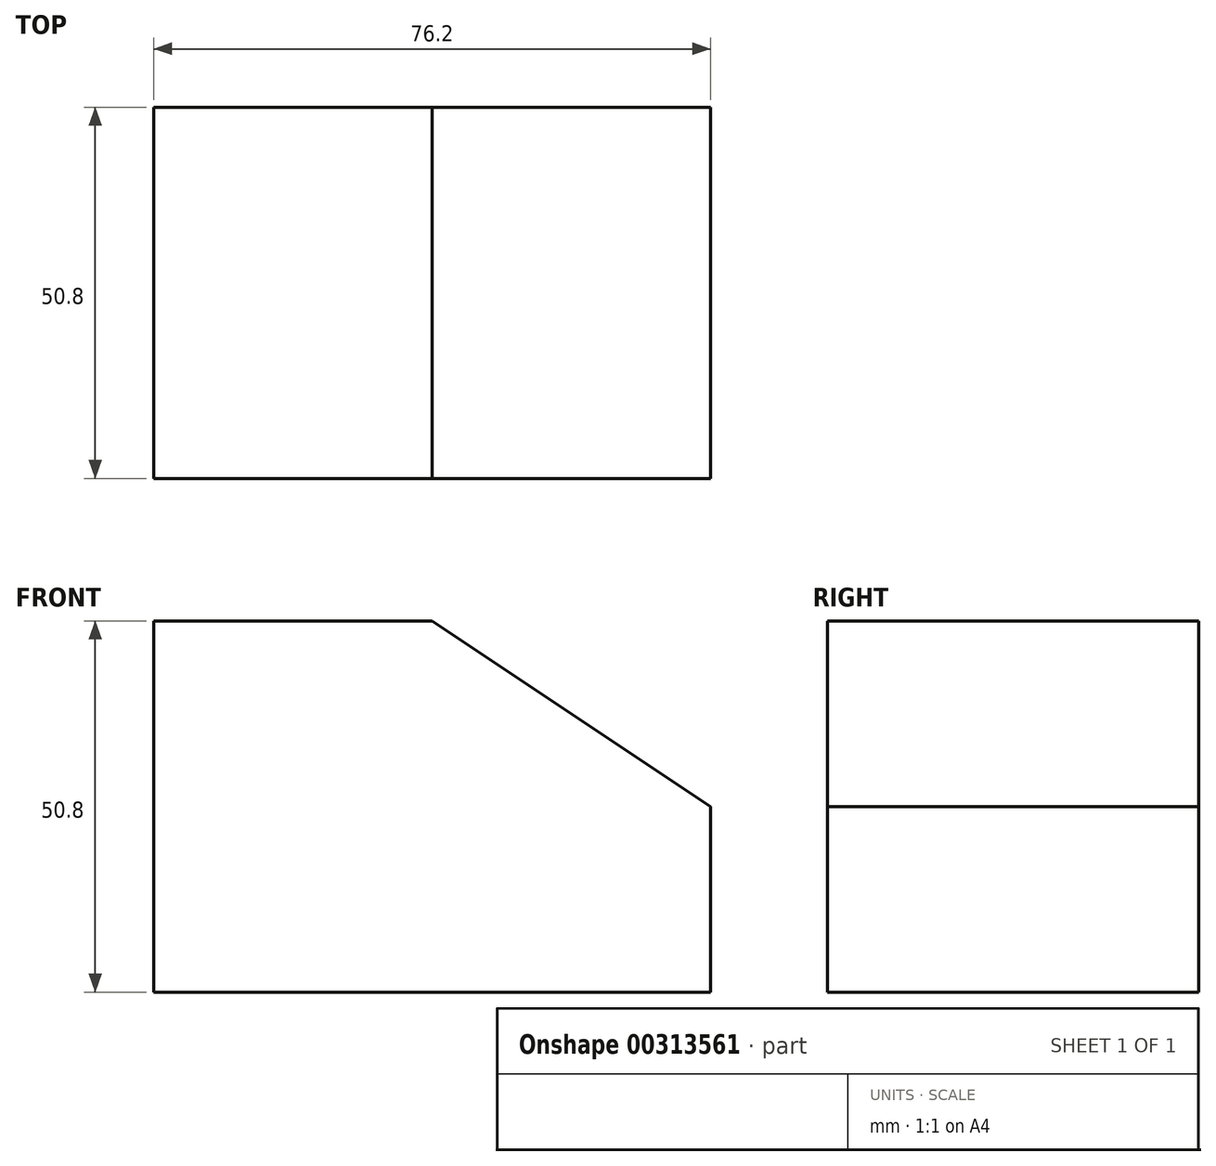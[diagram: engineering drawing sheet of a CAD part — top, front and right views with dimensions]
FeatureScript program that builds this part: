
annotation { "Feature Type Name" : "Feature", "Feature Type Description" : "" }
export const myFeature = defineFeature(function(context is Context, id is Id, definition is map)
    precondition{}
    {
        {
            var Q0;
            Q0=qCreatedBy(makeId("Front.planeOp"),FACE);
            var sketch = newSketch(context, id + "F0", { "sketchPlane" : qUnion([Q0])});
            skLineSegment(sketch, "E0", {"start": v(-32.06, -26.81) * mm, "end": v(44.14, -26.81) * mm});
            skLineSegment(sketch, "E1", {"start": v(44.14, -26.81) * mm, "end": v(44.14, -1.41) * mm});
            skLineSegment(sketch, "E2", {"start": v(-32.06, -26.81) * mm, "end": v(-32.06, 23.99) * mm});
            skLineSegment(sketch, "E3", {"start": v(-32.06, 23.99) * mm, "end": v(6.04, 23.99) * mm});
            skLineSegment(sketch, "E4", {"start": v(6.04, 23.99) * mm, "end": v(44.14, -1.41) * mm});
            skSolve(sketch);
        }
        {
            var Q0;
            Q0 = qSketchRegion(id + "F0", true);
            extrude(context, id + "F1", {"entities" : qUnion([Q0]), "depth" : 50.8 * mm});
        }
    });
